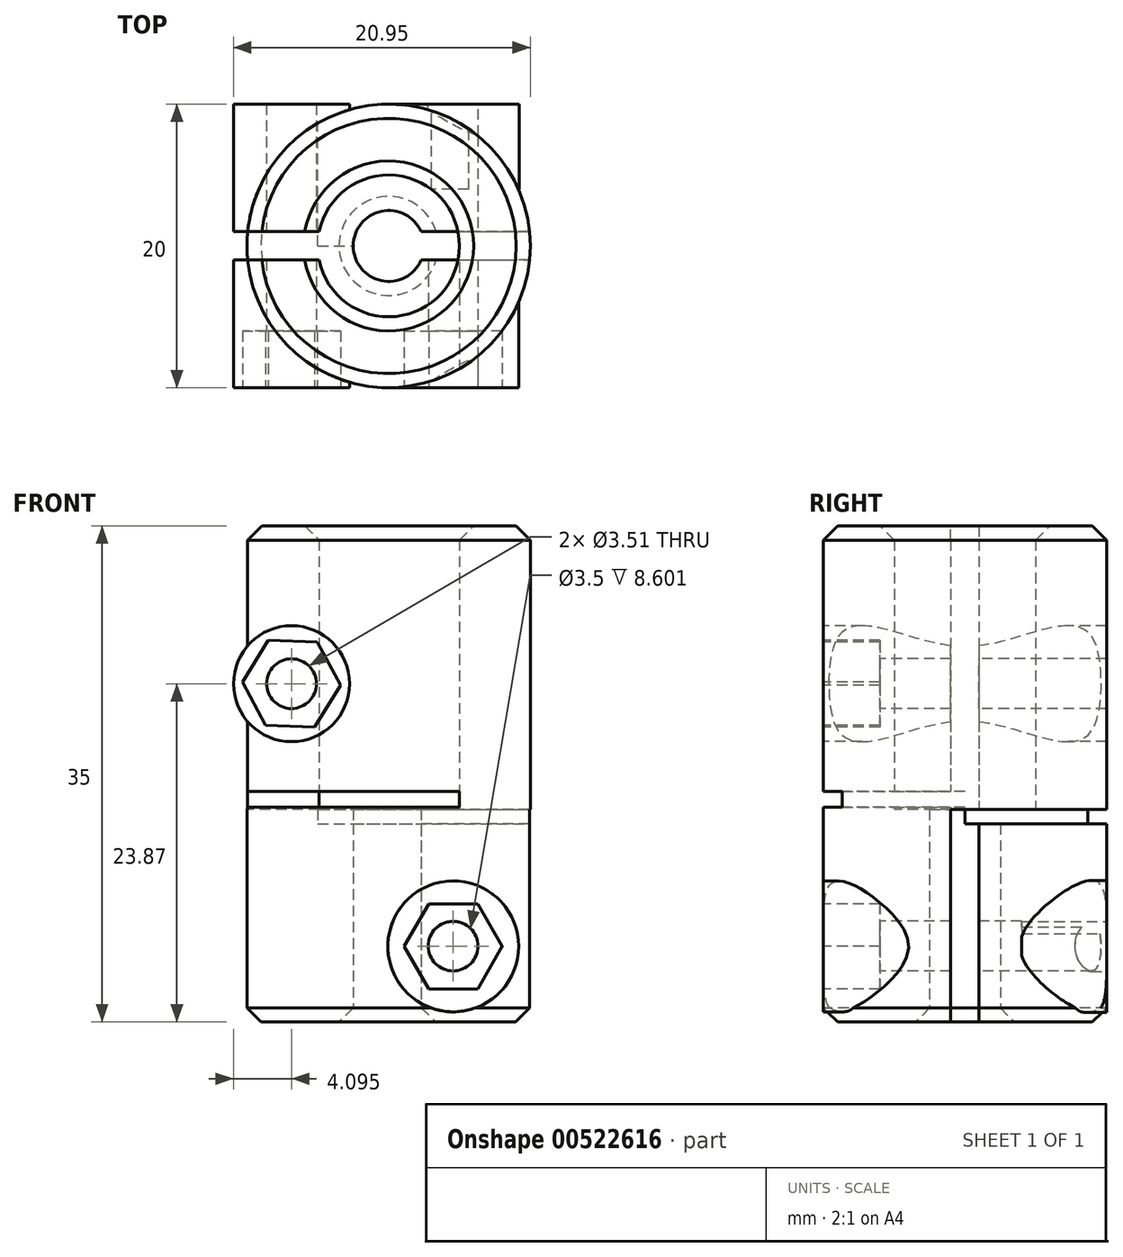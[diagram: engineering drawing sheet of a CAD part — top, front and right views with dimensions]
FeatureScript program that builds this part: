
annotation { "Feature Type Name" : "Feature", "Feature Type Description" : "" }
export const myFeature = defineFeature(function(context is Context, id is Id, definition is map)
    precondition{}
    {
        {
            var Q0;
            Q0=qCreatedBy(makeId("Top.planeOp"),FACE);
            var sketch = newSketch(context, id + "F0", { "sketchPlane" : qUnion([Q0])});
            skCircle(sketch, "E0", {"center": v(0, 0) * mm, "radius": 2.5 * mm});
            skCircle(sketch, "E1", {"center": v(0, 0) * mm, "radius": 10 * mm});
            skLineSegment(sketch, "E2", {"start": v(0, 0) * mm, "end": v(10, 0) * mm});
            skLineSegment(sketch, "E3.0", {"start": v(0, -1) * mm, "end": v(10, -1) * mm});
            skLineSegment(sketch, "E4.0", {"start": v(0, 1) * mm, "end": v(10, 1) * mm});
            skSolve(sketch);
        }
        {
            var Q0;
            {var subQ0=sQuery(id+"F0.wireOp",EDGE,"E4.0");var subQ1=sQuery(id+"F0.wireOp",EDGE,"E0");var subQ2=makeQuery(id+"F0.imprint","INTERSECT",VERTEX,{"derivedFrom":[subQ1,subQ0]});Q0=makeQuery(id+"F0.imprint","IMPRINT",FACE,{"disambiguationData":[TD([[makeQuery(id+"F0.imprint","IMPRINT",EDGE,{"disambiguationData":[TD([[subQ2,-1.0]])],"derivedFrom":subQ1}),-1.0]])]});}
            extrude(context, id + "F1", {"entities" : qUnion([Q0]), "depth" : 15 * mm});
        }
        {
            var Q0;
            Q0=makeQuery(id+"F1.opExtrude","CAP_FACE",FACE,{"disambiguationData":[OSD([sQuery(id+"F0.wireOp",EDGE,"E0"),sQuery(id+"F0.wireOp",EDGE,"E1"),sQuery(id+"F0.wireOp",EDGE,"E3.0"),sQuery(id+"F0.wireOp",EDGE,"E4.0")])],"isStart":false});
            var sketch = newSketch(context, id + "F2", { "sketchPlane" : qUnion([Q0])});
            skCircle(sketch, "E5", {"center": v(0, 0) * mm, "radius": 5 * mm});
            skLineSegment(sketch, "E6", {"start": v(-2.3, 1) * mm, "end": v(-9.95, 1) * mm});
            skLineSegment(sketch, "E7", {"start": v(2.3, -1) * mm, "end": v(-9.95, -1) * mm});
            skCircle(sketch, "E8", {"center": v(0, 0) * mm, "radius": 10 * mm});
            skLineSegment(sketch, "E9", {"start": v(-9.95, 1) * mm, "end": v(-12.38, 1) * mm});
            skLineSegment(sketch, "E10", {"start": v(-12.38, 1) * mm, "end": v(-12.38, -1) * mm});
            skLineSegment(sketch, "E11", {"start": v(-12.38, -1) * mm, "end": v(-9.95, -1) * mm});
            skSolve(sketch);
        }
        {
            var Q0;
            {var subQ0=sQuery(id+"F2.wireOp",EDGE,"E6");var subQ1=sQuery(id+"F2.wireOp",EDGE,"E5");var subQ2=makeQuery(id+"F2.imprint","INTERSECT",VERTEX,{"derivedFrom":[subQ1,subQ0]});Q0=makeQuery(id+"F2.imprint","IMPRINT",FACE,{"disambiguationData":[TD([[makeQuery(id+"F2.imprint","IMPRINT",EDGE,{"disambiguationData":[TD([[subQ2,1.0]])],"derivedFrom":subQ1}),-1.0]])]});}
            var Q1;
            {var subQ0=sQuery(id+"F2.wireOp",EDGE,"E5");var subQ1=makeQuery(id+"F1.opExtrude","CAP_EDGE",EDGE,{"disambiguationData":[OSD([sQuery(id+"F0.wireOp",EDGE,"E4.0")])],"isStart":false});var subQ2=makeQuery(id+"F2.imprint","INTERSECT",VERTEX,{"derivedFrom":[subQ1,subQ0]});Q1=makeQuery(id+"F2.imprint","IMPRINT",FACE,{"disambiguationData":[TD([[makeQuery(id+"F2.imprint","IMPRINT",EDGE,{"disambiguationData":[TD([[subQ2,1.0]])],"derivedFrom":subQ0}),-1.0]])]});}
            var Q2;
            {var subQ0=sQuery(id+"F2.wireOp",EDGE,"E7");var subQ1=sQuery(id+"F2.wireOp",EDGE,"E5");var subQ2=makeQuery(id+"F2.imprint","INTERSECT",VERTEX,{"derivedFrom":[subQ1,subQ0]});Q2=makeQuery(id+"F2.imprint","IMPRINT",FACE,{"disambiguationData":[TD([[makeQuery(id+"F2.imprint","IMPRINT",EDGE,{"disambiguationData":[TD([[subQ2,-1.0]])],"derivedFrom":subQ1}),-1.0]])]});}
            extrude(context, id + "F3", {"entities" : qUnion([Q0, Q1, Q2]), "operationType" : NewBodyOperationType.ADD, "depth" : 20 * mm});
        }
        {
            var Q0;
            Q0=qCreatedBy(makeId("Right.planeOp"),FACE);
            cPlane(context, id + "F4", {"entities" : qUnion([Q0]), "cplaneType" : CPlaneType.OFFSET, "offset" : 10 * mm, "width" : 150 * mm, "height" : 150 * mm});
        }
        {
            var Q0;
            Q0=qCreatedBy(id+"F4.planeOp",FACE);
            var sketch = newSketch(context, id + "F5", { "sketchPlane" : qUnion([Q0])});
            skLineSegment(sketch, "E12.bottom", {"start": v(0, 14.99) * mm, "end": v(10.11, 14.99) * mm});
            skLineSegment(sketch, "E12.top", {"start": v(0, 13.97) * mm, "end": v(10.11, 13.97) * mm});
            skLineSegment(sketch, "E12.left", {"start": v(0, 14.99) * mm, "end": v(0, 13.97) * mm});
            skLineSegment(sketch, "E12.right", {"start": v(10.11, 14.99) * mm, "end": v(10.11, 13.97) * mm});
            skSolve(sketch);
        }
        {
            var Q0;
            Q0=makeQuery(id+"F5.imprint","IMPRINT",FACE,{"disambiguationData":[TD([[makeQuery(id+"F5.imprint","IMPRINT",EDGE,{"derivedFrom":sQuery(id+"F5.wireOp",EDGE,"E12.bottom")}),-1.0]])]});
            extrude(context, id + "F6", {"entities" : qUnion([Q0]), "operationType" : NewBodyOperationType.REMOVE, "oppositeDirection" : true, "depth" : 15 * mm});
        }
        {
            var Q0;
            Q0=qCreatedBy(makeId("Right.planeOp"),FACE);
            cPlane(context, id + "F7", {"entities" : qUnion([Q0]), "cplaneType" : CPlaneType.OFFSET, "offset" : 10 * mm, "oppositeDirection" : true, "width" : 150 * mm, "height" : 150 * mm});
        }
        {
            var Q0;
            Q0=qCreatedBy(id+"F7.planeOp",FACE);
            var sketch = newSketch(context, id + "F8", { "sketchPlane" : qUnion([Q0])});
            skLineSegment(sketch, "E13.bottom", {"start": v(0, 15.15) * mm, "end": v(-11, 15.15) * mm});
            skLineSegment(sketch, "E13.top", {"start": v(0, 16.26) * mm, "end": v(-11, 16.26) * mm});
            skLineSegment(sketch, "E13.left", {"start": v(0, 15.15) * mm, "end": v(0, 16.26) * mm});
            skLineSegment(sketch, "E13.right", {"start": v(-11, 15.15) * mm, "end": v(-11, 16.26) * mm});
            skSolve(sketch);
        }
        {
            var Q0;
            Q0=makeQuery(id+"F8.imprint","IMPRINT",FACE,{"disambiguationData":[TD([[makeQuery(id+"F8.imprint","IMPRINT",EDGE,{"derivedFrom":sQuery(id+"F8.wireOp",EDGE,"E13.bottom")}),-1.0]])]});
            extrude(context, id + "F9", {"entities" : qUnion([Q0]), "operationType" : NewBodyOperationType.REMOVE, "depth" : 15 * mm});
        }
        {
            var Q0;
            Q0=qCreatedBy(makeId("Front.planeOp"),FACE);
            cPlane(context, id + "F10", {"entities" : qUnion([Q0]), "cplaneType" : CPlaneType.OFFSET, "offset" : 10 * mm, "width" : 150 * mm, "height" : 150 * mm});
        }
        {
            var Q0;
            Q0=qCreatedBy(id+"F10.planeOp",FACE);
            var sketch = newSketch(context, id + "F11", { "sketchPlane" : qUnion([Q0])});
            skCircle(sketch, "E14", {"center": v(4.55, 5.36) * mm, "radius": 1.75 * mm});
            skCircle(sketch, "E15", {"center": v(-6.86, 23.87) * mm, "radius": 1.76 * mm});
            skCircle(sketch, "E16", {"center": v(-6.86, 23.87) * mm, "radius": 4.09 * mm});
            skSolve(sketch);
        }
        {
            var Q0;
            Q0=qSketchRegion(id+"F11",true);
            extrude(context, id + "F12", {"entities" : qUnion([Q0]), "operationType" : NewBodyOperationType.ADD, "oppositeDirection" : true, "depth" : 20 * mm});
        }
        {
            var Q0;
            Q0=makeQuery(id+"F11.imprint","IMPRINT",FACE,{"disambiguationData":[TD([[makeQuery(id+"F11.imprint","IMPRINT",EDGE,{"derivedFrom":sQuery(id+"F11.wireOp",EDGE,"E15")}),1.0]])]});
            extrude(context, id + "F13", {"entities" : qUnion([Q0]), "operationType" : NewBodyOperationType.REMOVE, "oppositeDirection" : true, "depth" : 25 * mm});
        }
        {
            var Q0;
            Q0=makeQuery(id+"F11.imprint","IMPRINT",FACE,{"disambiguationData":[TD([[makeQuery(id+"F11.imprint","IMPRINT",EDGE,{"derivedFrom":sQuery(id+"F11.wireOp",EDGE,"E14")}),1.0]])]});
            extrude(context, id + "F14", {"entities" : qUnion([Q0]), "operationType" : NewBodyOperationType.REMOVE, "oppositeDirection" : true, "depth" : 25 * mm});
        }
        {
            var Q0;
            {var subQ0=sQuery(id+"F2.wireOp",EDGE,"E6");var subQ1=sQuery(id+"F2.wireOp",EDGE,"E5");var subQ2=makeQuery(id+"F2.imprint","INTERSECT",VERTEX,{"derivedFrom":[subQ1,subQ0]});Q0=makeQuery(id+"F2.imprint","IMPRINT",FACE,{"disambiguationData":[TD([[makeQuery(id+"F2.imprint","IMPRINT",EDGE,{"disambiguationData":[TD([[subQ2,1.0]])],"derivedFrom":subQ1}),1.0]])]});}
            var Q1;
            {var subQ0=sQuery(id+"F2.wireOp",EDGE,"E7");var subQ1=sQuery(id+"F2.wireOp",EDGE,"E5");var subQ2=makeQuery(id+"F2.imprint","INTERSECT",VERTEX,{"derivedFrom":[subQ1,subQ0]});Q1=makeQuery(id+"F2.imprint","IMPRINT",FACE,{"disambiguationData":[TD([[makeQuery(id+"F2.imprint","IMPRINT",EDGE,{"disambiguationData":[TD([[subQ2,-1.0]])],"derivedFrom":subQ1}),1.0]])]});}
            var Q2;
            {var subQ0=sQuery(id+"F2.wireOp",EDGE,"E6");var subQ1=sQuery(id+"F2.wireOp",EDGE,"E5");var subQ2=makeQuery(id+"F2.imprint","INTERSECT",VERTEX,{"derivedFrom":[subQ1,subQ0]});Q2=makeQuery(id+"F2.imprint","IMPRINT",FACE,{"disambiguationData":[TD([[makeQuery(id+"F2.imprint","IMPRINT",EDGE,{"disambiguationData":[TD([[subQ2,-1.0]])],"derivedFrom":subQ1}),-1.0]])]});}
            var Q3;
            {var subQ0=sQuery(id+"F2.wireOp",EDGE,"E6");var subQ1=sQuery(id+"F2.wireOp",EDGE,"E5");var subQ2=makeQuery(id+"F2.imprint","INTERSECT",VERTEX,{"derivedFrom":[subQ1,subQ0]});Q3=makeQuery(id+"F2.imprint","IMPRINT",FACE,{"disambiguationData":[TD([[makeQuery(id+"F2.imprint","IMPRINT",EDGE,{"disambiguationData":[TD([[subQ2,-1.0]])],"derivedFrom":subQ1}),1.0]])]});}
            extrude(context, id + "F15", {"entities" : qUnion([Q0, Q1, Q2, Q3]), "operationType" : NewBodyOperationType.REMOVE, "depth" : 25 * mm});
        }
        {
            var Q0;
            {var subQ0=sQuery(id+"F2.wireOp",EDGE,"E9");Q0=makeQuery(id+"F2.imprint","IMPRINT",FACE,{"disambiguationData":[TD([[makeQuery(id+"F2.imprint","IMPRINT",EDGE,{"derivedFrom":subQ0}),1.0]])]});}
            extrude(context, id + "F16", {"entities" : qUnion([Q0]), "operationType" : NewBodyOperationType.REMOVE, "depth" : 25 * mm});
        }
        {
            var Q0;
            Q0=makeQuery(id+"F12.opExtrude","CAP_FACE",FACE,{"disambiguationData":[OSD([sQuery(id+"F11.wireOp",EDGE,"E15"),sQuery(id+"F11.wireOp",EDGE,"E16")])],"isStart":true});
            var sketch = newSketch(context, id + "F17", { "sketchPlane" : qUnion([Q0])});
            skCircle(sketch, "E17.cCircle", {"center": v(-6.86, 23.87) * mm, "radius": 3 * mm, "construction": true});
            skLineSegment(sketch, "E17.0", {"start": v(-10.32, 23.98) * mm, "end": v(-8.49, 26.92) * mm});
            skLineSegment(sketch, "E17.1", {"start": v(-8.49, 26.92) * mm, "end": v(-5.03, 26.81) * mm});
            skLineSegment(sketch, "E17.2", {"start": v(-5.03, 26.81) * mm, "end": v(-3.4, 23.76) * mm});
            skLineSegment(sketch, "E17.3", {"start": v(-3.4, 23.76) * mm, "end": v(-5.22, 20.82) * mm});
            skLineSegment(sketch, "E17.4", {"start": v(-5.22, 20.82) * mm, "end": v(-8.68, 20.93) * mm});
            skLineSegment(sketch, "E17.5", {"start": v(-8.68, 20.93) * mm, "end": v(-10.32, 23.98) * mm});
            skPoint(sketch, "E17.0.midPoint", {"position": v(-9.4, 25.45) * mm});
            skCircle(sketch, "E18.cCircle", {"center": v(4.56, 5.34) * mm, "radius": 3 * mm, "construction": true});
            skLineSegment(sketch, "E18.0", {"start": v(2.83, 8.34) * mm, "end": v(6.3, 8.34) * mm});
            skLineSegment(sketch, "E18.1", {"start": v(6.3, 8.34) * mm, "end": v(8.02, 5.34) * mm});
            skLineSegment(sketch, "E18.2", {"start": v(8.02, 5.34) * mm, "end": v(6.3, 2.34) * mm});
            skLineSegment(sketch, "E18.3", {"start": v(6.3, 2.34) * mm, "end": v(2.83, 2.34) * mm});
            skLineSegment(sketch, "E18.4", {"start": v(2.83, 2.34) * mm, "end": v(1.1, 5.34) * mm});
            skLineSegment(sketch, "E18.5", {"start": v(1.1, 5.34) * mm, "end": v(2.83, 8.34) * mm});
            skPoint(sketch, "E18.0.midPoint", {"position": v(4.56, 8.34) * mm});
            skCircle(sketch, "E19", {"center": v(4.56, 5.34) * mm, "radius": 4.62 * mm});
            skSolve(sketch);
        }
        {
            var Q0;
            Q0=makeQuery(id+"F17.imprint","IMPRINT",FACE,{"disambiguationData":[TD([[makeQuery(id+"F17.imprint","IMPRINT",EDGE,{"derivedFrom":sQuery(id+"F17.wireOp",EDGE,"E18.0")}),-1.0]])]});
            var Q1;
            Q1=makeQuery(id+"F17.imprint","IMPRINT",FACE,{"disambiguationData":[TD([[makeQuery(id+"F17.imprint","IMPRINT",EDGE,{"derivedFrom":sQuery(id+"F17.wireOp",EDGE,"E17.0")}),-1.0]])]});
            extrude(context, id + "F18", {"entities" : qUnion([Q0, Q1]), "operationType" : NewBodyOperationType.REMOVE, "oppositeDirection" : true, "depth" : 4 * mm});
        }
        {
            var Q0;
            Q0=makeQuery(id+"F17.imprint","IMPRINT",FACE,{"disambiguationData":[TD([[makeQuery(id+"F17.imprint","IMPRINT",EDGE,{"derivedFrom":sQuery(id+"F17.wireOp",EDGE,"E18.0")}),1.0]])]});
            extrude(context, id + "F19", {"entities" : qUnion([Q0]), "operationType" : NewBodyOperationType.ADD, "oppositeDirection" : true, "depth" : 6.5 * mm});
        }
        {
            var Q0;
            Q0=qCreatedBy(makeId("Front.planeOp"),FACE);
            cPlane(context, id + "F20", {"entities" : qUnion([Q0]), "cplaneType" : CPlaneType.OFFSET, "offset" : 10 * mm, "oppositeDirection" : true, "width" : 150 * mm, "height" : 150 * mm});
        }
        {
            var Q0;
            Q0=qCreatedBy(id+"F20.planeOp",FACE);
            var sketch = newSketch(context, id + "F21", { "sketchPlane" : qUnion([Q0])});
            skCircle(sketch, "E20", {"center": v(4.55, 5.33) * mm, "radius": 1.77 * mm});
            skCircle(sketch, "E21", {"center": v(4.55, 5.33) * mm, "radius": 4.66 * mm});
            skSolve(sketch);
        }
        {
            var Q0;
            Q0=makeQuery(id+"F21.imprint","IMPRINT",FACE,{"disambiguationData":[TD([[makeQuery(id+"F21.imprint","IMPRINT",EDGE,{"derivedFrom":sQuery(id+"F21.wireOp",EDGE,"E20")}),-1.0]])]});
            extrude(context, id + "F22", {"entities" : qUnion([Q0]), "operationType" : NewBodyOperationType.ADD, "depth" : 6 * mm});
        }
        {
            var Q0;
            {var subQ0=sQuery(id+"F2.wireOp",EDGE,"E5");Q0=makeQuery(id+"F15.boolean.opBoolean","INTERSECT",EDGE,{"derivedFrom":[makeQuery(id+"F15.opExtrude","SWEPT_FACE",FACE,{"disambiguationData":[OSD([subQ0]),TDD([makeQuery(id+"F2.imprint","IMPRINT",EDGE,{"disambiguationData":[TD([[makeQuery(id+"F2.imprint","INTERSECT",VERTEX,{"derivedFrom":[subQ0,sQuery(id+"F2.wireOp",EDGE,"E6")]}),1.0]])],"derivedFrom":subQ0})])]}),makeQuery(id+"F15.opExtrude","SWEPT_FACE",FACE,{"disambiguationData":[OSD([subQ0]),TDD([makeQuery(id+"F2.imprint","IMPRINT",EDGE,{"disambiguationData":[TD([[makeQuery(id+"F2.imprint","INTERSECT",VERTEX,{"derivedFrom":[subQ0,sQuery(id+"F2.wireOp",EDGE,"E7")]}),-1.0]])],"derivedFrom":subQ0})])]})]});}
            chamfer(context, id + "F23", {"entities" : qUnion([Q0]), "width" : 1 * mm, "tangentPropagation" : true});
        }
        {
            var Q0;
            Q0=makeQuery(id+"F3.opExtrude","CAP_EDGE",EDGE,{"disambiguationData":[OSD([sQuery(id+"F2.wireOp",EDGE,"E8")])],"isStart":false});
            var Q1;
            Q1=makeQuery(id+"F1.opExtrude","CAP_EDGE",EDGE,{"disambiguationData":[OSD([sQuery(id+"F0.wireOp",EDGE,"E1")])],"isStart":true});
            var Q2;
            Q2=makeQuery(id+"F1.opExtrude","CAP_EDGE",EDGE,{"disambiguationData":[OSD([sQuery(id+"F0.wireOp",EDGE,"E0")])],"isStart":true});
            chamfer(context, id + "F24", {"entities" : qUnion([Q0, Q1, Q2]), "width" : 1 * mm, "tangentPropagation" : true});
        }
    });
